# Revit family: WAC_A3-Watson-Concrete-Sills
name_source: partatom
category: Specialty Equipment
revit_build: Autodesk Revit 2016 (Build: 20150220_1215(x64)
units: mm (PartAtom-declared; Revit-internal decimal feet)

## family parameters
Always vertical = Yes
Cut with Voids When Loaded = No
Host = Wall
Part Type = Normal
Room Calculation Point = No
Round Connector Dimension = Use Diameter
Shared = No

## types (3) — shared parameters

## per-type parameters (varying)
| type | Cill Depth | Cill Frame Height | Cill Frame Width | Cill Height Ext | Cill Height Int | Cill Length |
| Type P | 135 mm  [stored 0.442913 ft] | 15 mm  [stored 0.0492126 ft] | 25 mm  [stored 0.082021 ft] | 65 mm  [stored 0.213255 ft] | 100 mm  [stored 0.328084 ft] | 915 mm  [stored 3.00197 ft] |
| Type E Sills | 165 mm  [stored 0.541339 ft] | 15 mm  [stored 0.0492126 ft] | 15 mm  [stored 0.0492126 ft] | 50 mm  [stored 0.164042 ft] | 90 mm  [stored 0.295276 ft] | 1000 mm  [stored 3.28084 ft] |
| Type EV | 215 mm | 10 mm  [stored 0.0328084 ft] | 25 mm  [stored 0.082021 ft] | 60 mm  [stored 0.19685 ft] | 115 mm  [stored 0.377297 ft] | 1450 mm  [stored 4.75722 ft] |

note: [stored X ft] marks values corroborated as IEEE doubles in the binary element streams (Revit-internal decimal feet)

## geometry (parser evidence)
native form markers: Sweep x3
no freeform markers — native parametric forms only
